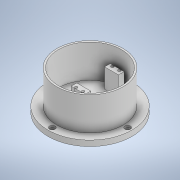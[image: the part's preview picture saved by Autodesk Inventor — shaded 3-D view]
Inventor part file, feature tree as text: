
AUTODESK INVENTOR PART (.ipt)
format: ipt  version: 2022 (Build 260153000, 153)  size: 242,688 bytes
history: native  units: in
note: dims shown in document units (in); Inventor stores cm internally (conversion verified against a paired STEP export)
features: extrude x8, sketch x8
ambient origin geometry x8: Origin, YZ Plane, XZ Plane, XY Plane, X Axis, Y Axis, Z Axis, Center Point
bodies: Solid1 (feature_tree)
feature tree (16):
  extrude  "Extrusion1"  Depth=0.315in TaperAngle=0.0deg
  extrude  "Extrusion2"  Depth=0.1969in
  extrude  "Extrusion3"  Depth=0.1969in
  extrude  "Extrusion4"  Depth=0.1969in
  extrude  "Extrusion5"  Depth=0.1969in
  extrude  "Extrusion6"  Depth=0.315in
  extrude  "Extrusion7"  Depth=0.1969in
  extrude  "Extrusion8"  Depth=0.1969in
  sketch  "Sketch1"  dims[d0=4.7244in d1=0.315in d2=0.0in]
  sketch  "Sketch2"  dims[d3=0.315in d4=0.1969in]
  sketch  "Sketch3"  dims[d5=0.315in d6=0.1969in]
  sketch  "Sketch4"  dims[d7=0.315in d8=0.1969in]
  sketch  "Sketch5"  dims[d9=0.315in d10=0.1969in]
  sketch  "Sketch6"  dims[d11=0.315in d12=0.0in d13=0.315in]
  sketch  "Sketch7"  dims[d14=0.315in d15=0.1969in]
  sketch  "Sketch8"  dims[d16=0.315in d17=0.1969in d18=0.315in d19=0.1181in d20=0.0in d21=3.7402in d22=3.5433in d23=0.3937in d24=0.3543in d25=0.3937in d26=0.2756in d27=1.8701in d28=0.0in d29=0.3937in d30=0.3543in d31=0.7874in d32=0.2756in d33=1.5748in d34=0.315in d35=0.315in d36=0.315in d37=1.1024in d38=0.0in d39=0.1575in d40=0.1575in d41=1.1024in d42=0.0in d43=0.8661in d44=0.0in d45=0.0787in d46=0.1969in d47=0.1969in d48=0.1575in d49=0.1575in d50=0.0787in d51=0.1575in d52=0.1575in d53=0.3937in d54=0.0in]
